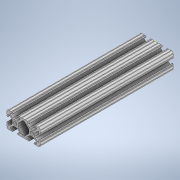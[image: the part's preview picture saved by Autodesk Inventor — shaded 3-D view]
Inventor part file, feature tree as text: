
AUTODESK INVENTOR PART (.ipt)
format: ipt  version: 2020 (Build 240168000, 168)  size: 333,312 bytes
history: native  units: in
note: dims shown in document units (in); Inventor stores cm internally (conversion verified against a paired STEP export)
features: sketch x2, extrude x1
ambient origin geometry x8: Origin, YZ Plane, XZ Plane, XY Plane, X Axis, Y Axis, Z Axis, Center Point
bodies: Solid1 (feature_tree)
feature tree (3):
  extrude  "Extrusion1"  [1 undecoded]
  sketch  "Sketch2"
  sketch  "Sketch1"  dims[d0=8.0in d1=0.0in]
note: 1 required parameter value undecoded (feature->parameter linkage not recoverable at this tier; creation-order binding heuristic only, values carry confidence <= 0.55)
